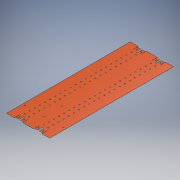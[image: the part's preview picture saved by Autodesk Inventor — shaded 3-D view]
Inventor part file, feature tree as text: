
AUTODESK INVENTOR PART (.ipt)
format: ipt  version: 2019 (Build 230136000, 136)  size: 403,968 bytes
history: native  units: mm
features: mirror x5, extrude x4, other x4
ambient origin geometry x8: Origin, YZ Plane, XZ Plane, XY Plane, X Axis, Y Axis, Z Axis, Center Point
bodies: Solid1 (feature_tree)
feature tree (13):
  extrude  "Skin Body"  Depth=1494.0mm
  extrude  "Feature Cut"  Depth=747.0mm
  mirror  "Feature Cut Side Mirror"
  mirror  "Feature Cut Mirror"
  extrude  "End Cut"  Depth=424.0mm
  mirror  "End Cut Mirror"
  extrude  "Slot Cut"  Depth=212.0mm
  mirror  "Slot Cut Side Mirror"
  mirror  "Slot Cut Mirror"
  other  "Skin Scheme"
  other  "Feature Cut Outline"
  other  "End Cut Outline"
  other  "Slot Cut Outline"
